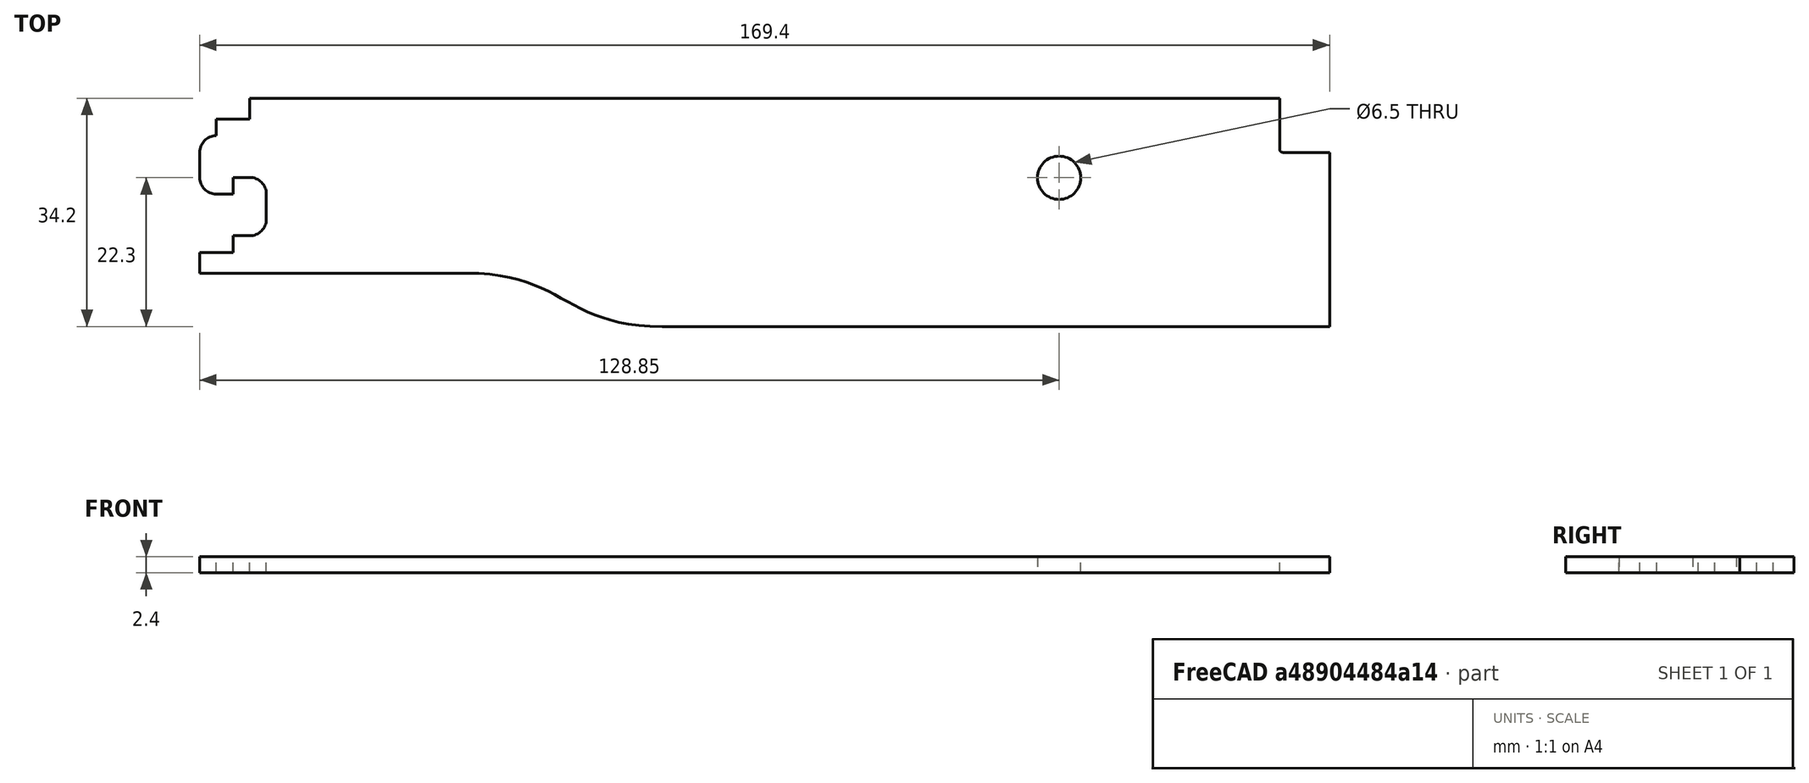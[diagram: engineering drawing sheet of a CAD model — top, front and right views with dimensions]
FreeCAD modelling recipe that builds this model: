
FCSTD DOCUMENT  (FreeCAD 0.19R0.19.2)
Label: v0_26
License: All rights reserved
LicenseURL: http://en.wikipedia.org/wiki/All_rights_reserved
objects: Sketcher::SketchObject×1, Part::Extrusion×1
note: 2 computed .brp shape members not serialized (recipe doc carries the construction recipe); baked Part::Feature solids carry a one-line shape summary decoded from their .brp

FEATURE [Sketcher::SketchObject] Sketch
  FullyConstrained = true
  sketch-geometry (33):
    g0: LineSegment StartX=0 StartY=0 StartZ=0 EndX=154.4 EndY=0 EndZ=0
    g1: Circle CenterX=121.35 CenterY=-11.9 CenterZ=0 NormalX=0 NormalY=0 NormalZ=1 AngleXU=0 Radius=3.25
    g2: LineSegment StartX=154.4 StartY=0 StartZ=0 EndX=154.4 EndY=-7.6 EndZ=0
    g3: ArcOfCircle CenterX=154.9 CenterY=-7.6 CenterZ=0 NormalX=0 NormalY=0 NormalZ=1 AngleXU=0 Radius=0.5 StartAngle=3.14159 EndAngle=4.71239
    g4: LineSegment StartX=-5 StartY=-3.1 StartZ=0 EndX=0 EndY=-3.1 EndZ=0
    g5: LineSegment StartX=-5 StartY=-3.1 StartZ=0 EndX=-5 EndY=-5.6 EndZ=0
    g6: LineSegment StartX=-7.5 StartY=-8.1 StartZ=0 EndX=-7.5 EndY=-11.85 EndZ=0
    g7: ArcOfCircle CenterX=-5 CenterY=-8.1 CenterZ=0 NormalX=0 NormalY=0 NormalZ=1 AngleXU=0 Radius=2.5 StartAngle=1.5708 EndAngle=3.14159
    g8: LineSegment StartX=-5 StartY=-14.35 StartZ=0 EndX=-2.5 EndY=-14.35 EndZ=0
    g9: ArcOfCircle CenterX=-5 CenterY=-11.85 CenterZ=0 NormalX=0 NormalY=0 NormalZ=1 AngleXU=0 Radius=2.5 StartAngle=3.14159 EndAngle=4.71239
    g10: LineSegment StartX=-2.5 StartY=-14.35 StartZ=0 EndX=-2.5 EndY=-11.85 EndZ=0
    g11: LineSegment StartX=-2.5 StartY=-11.85 StartZ=0 EndX=1.492e-13 EndY=-11.85 EndZ=0
    g12: ArcOfCircle CenterX=1.492e-13 CenterY=-14.35 CenterZ=0 NormalX=0 NormalY=0 NormalZ=1 AngleXU=0 Radius=2.5 StartAngle=8e-16 EndAngle=1.5708
    g13: LineSegment StartX=2.5 StartY=-14.35 StartZ=0 EndX=2.5 EndY=-18.1 EndZ=0
    g14: ArcOfCircle CenterX=1.474e-13 CenterY=-18.1 CenterZ=0 NormalX=0 NormalY=0 NormalZ=1 AngleXU=0 Radius=2.5 StartAngle=4.71239 EndAngle=6.28319
    g15: LineSegment StartX=-2.5 StartY=-20.6 StartZ=0 EndX=1.47e-13 EndY=-20.6 EndZ=0
    g16: LineSegment StartX=-2.5 StartY=-20.6 StartZ=0 EndX=-2.5 EndY=-23.1 EndZ=0
    g17: LineSegment StartX=-7.5 StartY=-23.1 StartZ=0 EndX=-2.5 EndY=-23.1 EndZ=0
    g18: LineSegment StartX=32.5209 StartY=-26.2 StartZ=0 EndX=-7.5 EndY=-26.2 EndZ=0
    g19: LineSegment StartX=61.85 StartY=-34.2 StartZ=0 EndX=161.9 EndY=-34.2 EndZ=0
    g20: LineSegment StartX=161.9 StartY=-8.1 StartZ=0 EndX=161.9 EndY=-34.2 EndZ=0
    g21: LineSegment StartX=154.9 StartY=-8.1 StartZ=0 EndX=161.9 EndY=-8.1 EndZ=0
    g22: LineSegment StartX=-7.5 StartY=-23.1 StartZ=0 EndX=-7.5 EndY=-26.2 EndZ=0
    g23: LineSegment StartX=0 StartY=0 StartZ=0 EndX=0 EndY=-3.1 EndZ=0
    g24-g28: Circle x5 (B-spline internal-alignment scaffolding for g29; pole/knot coordinates omitted)
    g29: BSplineCurve PolesCount=5 KnotsCount=3 Degree=3 IsPeriodic=0
    g30: GeomPoint X=61.85 Y=-34.2 Z=0
    g31: GeomPoint X=47.185 Y=-30.2 Z=0
    g32: GeomPoint X=32.5209 Y=-26.2 Z=0
  constraints (67):
    c: PointOnObject(g0,g-2)
    c: Horizontal(g0)
    c: Distance(g0) = 154.4
    c: DistanceY(g-1,g0) = 0
    c: Block(g1)
    c: Vertical(g2)
    c: Distance(g2) = 7.6
    c: Coincident(g2,g0)
    c: Block(g3)
    c: Horizontal(g4)
    c: Vertical(g5)
    c: Coincident(g5,g4)
    c: Vertical(g6)
    c: Coincident(g7,g5)
    c: Block(g7)
    c: Coincident(g6,g7)
    c: Horizontal(g8)
    c: Coincident(g9,g6)
    c: Block(g9)
    c: Block(g8)
    c: Vertical(g10)
    c: Coincident(g10,g8)
    c: Horizontal(g11)
    c: Coincident(g11,g10)
    c: Coincident(g12,g11)
    c: Vertical(g13)
    c: Block(g12)
    c: Coincident(g13,g12)
    c: Coincident(g14,g13)
    c: Block(g14)
    c: Horizontal(g15)
    c: Coincident(g15,g14)
    c: Vertical(g16)
    c: Coincident(g16,g15)
    c: Horizontal(g17)
    c: Coincident(g17,g16)
    c: Block(g16)
    c: Block(g4)
    c: Horizontal(g19)
    c: Horizontal(g18)
    c: Block(g18)
    c: Block(g19)
    c: Vertical(g20)
    c: Distance(g20) = 26.1
    c: Coincident(g20,g19)
    c: Horizontal(g21)
    c: Coincident(g21,g20)
    c: Coincident(g21,g3)
    c: Distance(g21) = 7
    c: Distance(g16) = 2.5
    c: Distance(g16) = 2.5
    c: Block(g17)
    c: Vertical(g22)
    c: Coincident(g22,g17)
    c: Coincident(g22,g18)
    c: Vertical(g23)
    c: Coincident(g23,g0)
    c: Coincident(g23,g4)
    c: Coincident(g29,g19)
    c: Weight(g24) = 1
    c: Equal(g24, g25-g28) x4
    c: Coincident(g29,g18)
    c: InternalAlignment(g24-g28 -> g29) x5
    c: InternalAlignment(g30,g29)
    c: InternalAlignment(g31,g29)
    c: InternalAlignment(g32,g29)
    c: Block(g29)
FEATURE [Part::Extrusion] Extrude
  Base = -> Sketch
  Dir = (0,0,1)
  DirMode = 2
  FaceMakerClass = Part::FaceMakerBullseye
  LengthFwd = 2.4
  LengthRev = 0
  Solid = true
  Symmetric = false
